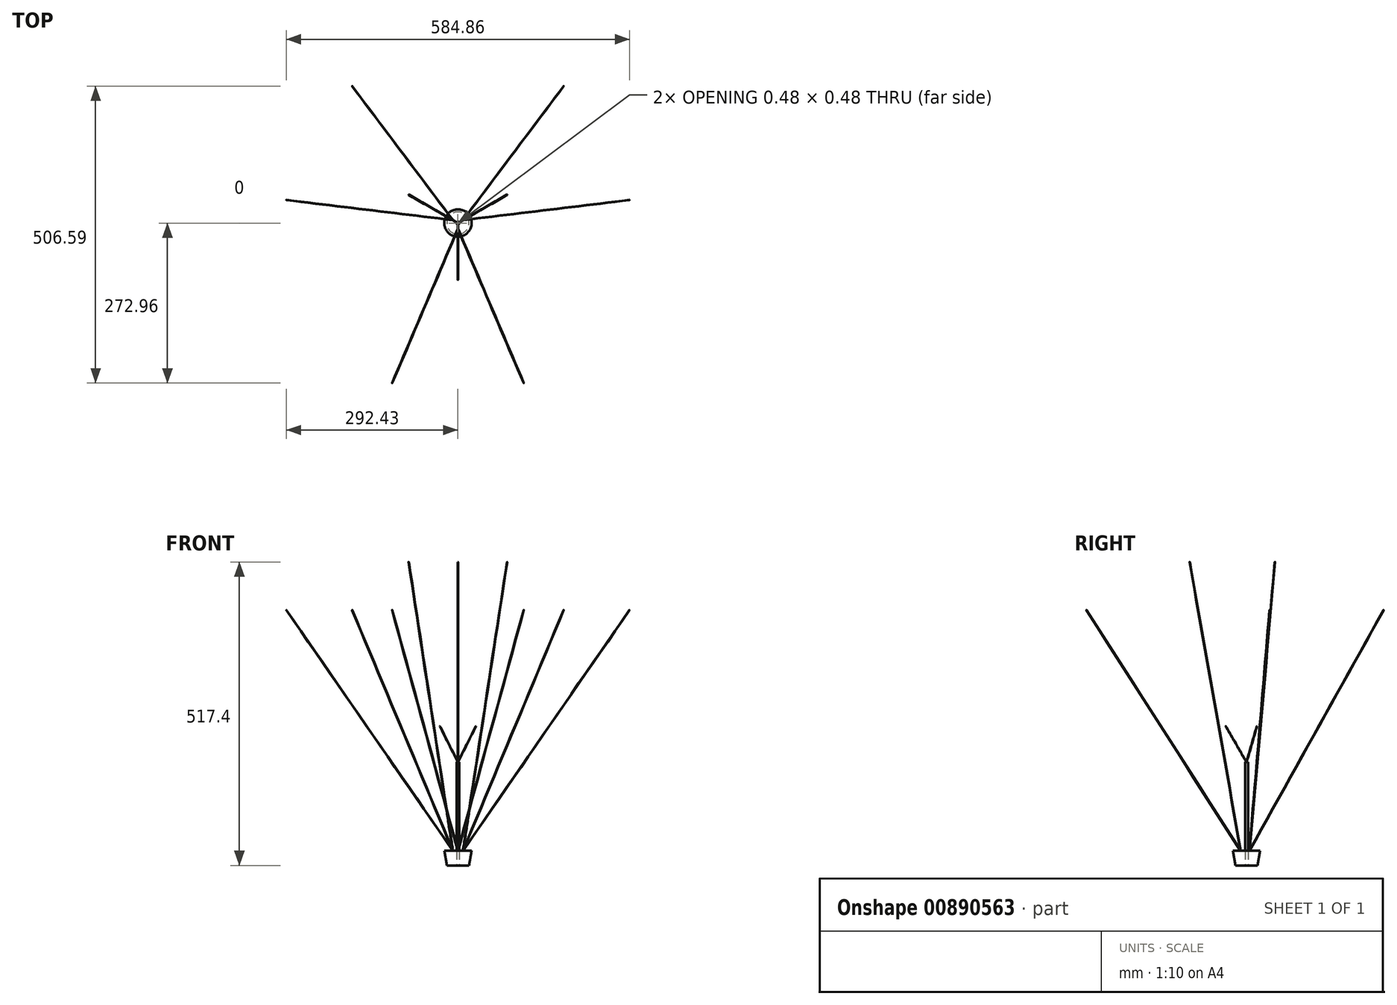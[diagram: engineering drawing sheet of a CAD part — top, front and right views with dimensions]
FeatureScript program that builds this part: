
annotation { "Feature Type Name" : "Feature", "Feature Type Description" : "" }
export const myFeature = defineFeature(function(context is Context, id is Id, definition is map)
    precondition{}
    {
        {
            var Q0;
            Q0=qCreatedBy(makeId("Top.planeOp"),FACE);
            var sketch = newSketch(context, id + "F0", { "sketchPlane" : qUnion([Q0])});
            skLineSegment(sketch, "E0", {"start": v(0, 0) * mm, "end": v(0, -141.4) * mm});
            skCircle(sketch, "E1", {"center": v(0, -141.4) * mm, "radius": 50.06 * mm});
            skSolve(sketch);
        }
        {
            var Q0;
            Q0=sQuery(id+"F0.wireOp",EDGE,"E0");
            extrude(context, id + "F1", {"bodyType" : ToolBodyType.SURFACE, "surfaceEntities" : qUnion([Q0]), "endBound" : BoundingType.SYMMETRIC, "depth" : 1 * mm, "offsetDistance" : 25 * mm});
        }
        {
            var Q0;
            Q0=makeQuery(id+"F0.imprint","IMPRINT",FACE,{"disambiguationData":[TD([[makeQuery(id+"F0.imprint","IMPRINT",EDGE,{"derivedFrom":sQuery(id+"F0.wireOp",EDGE,"E1")}),1.0]])]});
            var Q1;
            Q1=sQuery(id+"F0.wireOp",EDGE,"E1");
            extrude(context, id + "F2", {"entities" : qUnion([Q0]), "bodyType" : ToolBodyType.SURFACE, "surfaceEntities" : qUnion([Q1]), "depth" : 1 * mm, "offsetDistance" : 25 * mm});
        }
        {
            var Q0;
            Q0=makeQuery(id+"F1.opExtrude","SWEPT_EDGE",EDGE,{"disambiguationData":[OSD([sQuery(id+"F0.wireOp",VERTEX,"E0.end")])]});
            cPoint(context, id + "F3", {"entities" : qUnion([Q0]), "parameter" : 0.5});
        }
        {
            var Q0;
            Q0=makeQuery(id+"F2.opExtrude","SWEPT_BODY",BODY,{"disambiguationData":[OSD([sQuery(id+"F0.wireOp",EDGE,"E1")])]});
            var Q1;
            Q1=qCreatedBy(id+"F3",VERTEX);
            transform(context, id + "F4", {"entities" : qUnion([Q0]), "transformType" : TransformType.TRANSLATION_3D, "dx" : 0 * mm, "dy" : 0 * mm, "dz" : 5 * mm, "makeCopy" : false});
        }
        {
            var Q0;
            Q0=makeQuery(id+"F2.opExtrude","SWEPT_BODY",BODY,{"disambiguationData":[OSD([sQuery(id+"F0.wireOp",EDGE,"E1")])]});
            var Q1;
            Q1=qCreatedBy(makeId("Top.planeOp"),FACE);
            mirror(context, id + "F5", {"entities" : qUnion([Q0]), "mirrorPlane" : qUnion([Q1])});
        }
        {
            var Q0;
            Q0=makeQuery(id+"F1.opExtrude","SWEPT_BODY",BODY,{"disambiguationData":[OSD([sQuery(id+"F0.wireOp",EDGE,"E0")])]});
            var Q1;
            Q1=makeQuery(id+"F2.opExtrude","SWEPT_BODY",BODY,{"disambiguationData":[OSD([sQuery(id+"F0.wireOp",EDGE,"E1")])]});
            var Q2;
            Q2=makeQuery(id+"F5.opPattern","COPY",BODY,{"derivedFrom":makeQuery(id+"F2.opExtrude","SWEPT_BODY",BODY,{"disambiguationData":[OSD([sQuery(id+"F0.wireOp",EDGE,"E1")])]}),"instanceName":"1"});
            var Q3;
            Q3=makeQuery(id+"F1.opExtrude","SWEPT_EDGE",EDGE,{"disambiguationData":[OSD([sQuery(id+"F0.wireOp",VERTEX,"E0.start")])]});
            circularPattern(context, id + "F6", {"entities" : qUnion([Q0, Q1, Q2]), "axis" : qUnion([Q3]), "angle" : 360 * degree, "instanceCount" : 6, "equalSpace" : true});
        }
        {
            var Q0;
            Q0=qCreatedBy(makeId("Top.planeOp"),FACE);
            var sketch = newSketch(context, id + "F7", { "sketchPlane" : qUnion([Q0])});
            skCircle(sketch, "E2", {"center": v(0, 0) * mm, "radius": 2.5 * mm});
            skSolve(sketch);
        }
        {
            var Q0;
            Q0=qSketchRegion(id+"F7",true);
            extrude(context, id + "F8", {"entities" : qUnion([Q0]), "depth" : 176 * mm, "offsetDistance" : 25 * mm});
        }
        {
            var Q0;
            Q0=makeQuery(id+"F8.opExtrude","CAP_FACE",FACE,{"disambiguationData":[OSD([sQuery(id+"F7.wireOp",EDGE,"E2")])],"isStart":false});
            cPlane(context, id + "F9", {"entities" : qUnion([Q0]), "cplaneType" : CPlaneType.OFFSET, "offset" : 0 * mm, "width" : 150 * mm, "height" : 150 * mm});
        }
        {
            var Q0;
            Q0=qCreatedBy(makeId("Right.planeOp"),FACE);
            var sketch = newSketch(context, id + "F10", { "sketchPlane" : qUnion([Q0])});
            skLineSegment(sketch, "E3.0", {"start": v(-2.5, 176) * mm, "end": v(2.5, 176) * mm, "construction": true});
            skPoint(sketch, "E4", {"position": v(0, 176) * mm});
            skLineSegment(sketch, "E5", {"start": v(0, 176) * mm, "end": v(-35.41, 237.34) * mm});
            skLineSegment(sketch, "E6", {"start": v(0, 176) * mm, "end": v(0, 197.2) * mm, "construction": true});
            skArc(sketch, "E7", {"start": v(0, 265.25) * mm, "mid": v(-28.43, 264.9) * mm, "end": v(-35.41, 237.34) * mm});
            skLineSegment(sketch, "E8", {"start": v(0, 265.25) * mm, "end": v(16.1, 265.25) * mm, "construction": true});
            skSolve(sketch);
        }
        {
            var Q0;
            Q0=qCreatedBy(id+"F9.planeOp",FACE);
            var sketch = newSketch(context, id + "F11", { "sketchPlane" : qUnion([Q0])});
            skCircle(sketch, "E9", {"center": v(0, 0) * mm, "radius": 0.25 * mm});
            skSolve(sketch);
        }
        {
            var Q0;
            Q0=makeQuery(id+"F11.imprint","IMPRINT",FACE,{"disambiguationData":[TD([[makeQuery(id+"F11.imprint","IMPRINT",EDGE,{"derivedFrom":sQuery(id+"F11.wireOp",EDGE,"E9")}),1.0]])]});
            var Q1;
            Q1=sQuery(id+"F10.wireOp",EDGE,"E5");
            sweep(context, id + "F12", {"operationType" : NewBodyOperationType.ADD, "profiles" : qUnion([Q0]), "path" : qUnion([Q1]), "keepProfileOrientation" : true});
        }
        {
            var Q0;
            Q0=makeQuery(id+"F8.opExtrude","SWEPT_BODY",BODY,{"disambiguationData":[OSD([sQuery(id+"F7.wireOp",EDGE,"E2")])]});
            var Q1;
            Q1=makeQuery(id+"F8.opExtrude","SWEPT_FACE",FACE,{"disambiguationData":[OSD([sQuery(id+"F7.wireOp",EDGE,"E2")])]});
            circularPattern(context, id + "F13", {"entities" : qUnion([Q0]), "axis" : qUnion([Q1]), "angle" : 360 * degree, "instanceCount" : 3, "equalSpace" : true});
        }
        {
            var Q0;
            Q0=sQuery(id+"F10.wireOp",EDGE,"E7");
            var Q1;
            Q1=makeQuery(id+"F8.opExtrude","SWEPT_FACE",FACE,{"disambiguationData":[OSD([sQuery(id+"F7.wireOp",EDGE,"E2")])]});
            revolve(context, id + "F14", {"bodyType" : ToolBodyType.SURFACE, "surfaceOperationType" : NewSurfaceOperationType.NEW, "surfaceEntities" : qUnion([Q0]), "axis" : qUnion([Q1]), "revolveType" : RevolveType.FULL});
        }
        {
            var Q0;
            Q0=qCreatedBy(makeId("Top.planeOp"),FACE);
            var sketch = newSketch(context, id + "F15", { "sketchPlane" : qUnion([Q0])});
            skCircle(sketch, "E10", {"center": v(0, 0) * mm, "radius": 18.9 * mm});
            skSolve(sketch);
        }
        {
            var Q0;
            Q0=makeQuery(id+"F15.imprint","IMPRINT",FACE,{"disambiguationData":[TD([[makeQuery(id+"F15.imprint","IMPRINT",EDGE,{"derivedFrom":sQuery(id+"F15.wireOp",EDGE,"E10")}),1.0]])]});
            extrude(context, id + "F16", {"entities" : qUnion([Q0]), "depth" : 25 * mm, "offsetDistance" : 25 * mm, "hasDraft" : true, "draftAngle" : 10 * degree});
        }
        {
            var Q0;
            Q0=qCreatedBy(makeId("Right.planeOp"),FACE);
            var sketch = newSketch(context, id + "F17", { "sketchPlane" : qUnion([Q0])});
            skPoint(sketch, "E11", {"position": v(-10, 25) * mm});
            skLineSegment(sketch, "E12", {"start": v(-10, 25) * mm, "end": v(-96.82, 517.4) * mm});
            skLineSegment(sketch, "E13", {"start": v(-10, 25) * mm, "end": v(-252.21, 544.42) * mm, "construction": true});
            skArc(sketch, "E14", {"start": v(-96.82, 517.4) * mm, "mid": v(-165.36, 587.27) * mm, "end": v(-259.14, 559.3) * mm});
            skSolve(sketch);
        }
        {
            var Q0;
            Q0=makeQuery(id+"F16.opExtrude","CAP_FACE",FACE,{"disambiguationData":[OSD([sQuery(id+"F15.wireOp",EDGE,"E10")])],"isStart":false});
            var sketch = newSketch(context, id + "F18", { "sketchPlane" : qUnion([Q0])});
            skCircle(sketch, "E15", {"center": v(0, -10) * mm, "radius": 0.25 * mm});
            skSolve(sketch);
        }
        {
            var Q0;
            Q0=qSketchRegion(id+"F18",true);
            var Q1;
            Q1=sQuery(id+"F17.wireOp",EDGE,"E12");
            sweep(context, id + "F19", {"profiles" : qUnion([Q0]), "path" : qUnion([Q1])});
        }
        {
            var Q0;
            Q0=makeQuery(id+"F19.opSweep","SWEPT_BODY",BODY,{"disambiguationData":[OSD([sQuery(id+"F17.wireOp",EDGE,"E12"),sQuery(id+"F18.wireOp",EDGE,"E15")])]});
            var Q1;
            Q1=sQuery(id+"F17.wireOp",EDGE,"E13");
            circularPattern(context, id + "F20", {"entities" : qUnion([Q0]), "axis" : qUnion([Q1]), "angle" : 360 * degree, "instanceCount" : 3, "equalSpace" : true});
        }
        {
            var Q0;
            Q0=sQuery(id+"F17.wireOp",EDGE,"E14");
            var Q1;
            Q1=sQuery(id+"F17.wireOp",EDGE,"E13");
            revolve(context, id + "F21", {"bodyType" : ToolBodyType.SURFACE, "surfaceOperationType" : NewSurfaceOperationType.NEW, "surfaceEntities" : qUnion([Q0]), "axis" : qUnion([Q1]), "revolveType" : RevolveType.FULL});
        }
        {
            var Q0;
            Q0=makeQuery(id+"F20.opPattern","COPY",BODY,{"derivedFrom":makeQuery(id+"F16.opExtrude","SWEPT_BODY",BODY,{"disambiguationData":[OSD([sQuery(id+"F15.wireOp",EDGE,"E10")])]}),"instanceName":"2"});
            var Q1;
            Q1=makeQuery(id+"F20.opPattern","COPY",BODY,{"derivedFrom":makeQuery(id+"F16.opExtrude","SWEPT_BODY",BODY,{"disambiguationData":[OSD([sQuery(id+"F15.wireOp",EDGE,"E10")])]}),"instanceName":"1"});
            var Q2;
            Q2=makeQuery(id+"F21.opRevolve","SWEPT_BODY",BODY,{"disambiguationData":[OSD([sQuery(id+"F17.wireOp",EDGE,"E14")])]});
            var Q3;
            Q3=makeQuery(id+"F8.opExtrude","SWEPT_BODY",BODY,{"disambiguationData":[OSD([sQuery(id+"F7.wireOp",EDGE,"E2")])]});
            var Q4;
            Q4=makeQuery(id+"F19.opSweep","SWEPT_BODY",BODY,{"disambiguationData":[OSD([sQuery(id+"F17.wireOp",EDGE,"E12"),sQuery(id+"F18.wireOp",EDGE,"E15")])]});
            var Q5;
            Q5=makeQuery(id+"F20.opPattern","COPY",BODY,{"derivedFrom":makeQuery(id+"F19.opSweep","SWEPT_BODY",BODY,{"disambiguationData":[OSD([sQuery(id+"F17.wireOp",EDGE,"E12"),sQuery(id+"F18.wireOp",EDGE,"E15")])]}),"instanceName":"1"});
            var Q6;
            Q6=makeQuery(id+"F20.opPattern","COPY",BODY,{"derivedFrom":makeQuery(id+"F19.opSweep","SWEPT_BODY",BODY,{"disambiguationData":[OSD([sQuery(id+"F17.wireOp",EDGE,"E12"),sQuery(id+"F18.wireOp",EDGE,"E15")])]}),"instanceName":"2"});
            var Q7;
            Q7=makeQuery(id+"F8.opExtrude","SWEPT_FACE",FACE,{"disambiguationData":[OSD([sQuery(id+"F7.wireOp",EDGE,"E2")])]});
            circularPattern(context, id + "F22", {"entities" : qUnion([Q0, Q1, Q2, Q3, Q4, Q5, Q6]), "axis" : qUnion([Q7]), "angle" : 360 * degree, "instanceCount" : 3, "equalSpace" : true});
        }
    });
